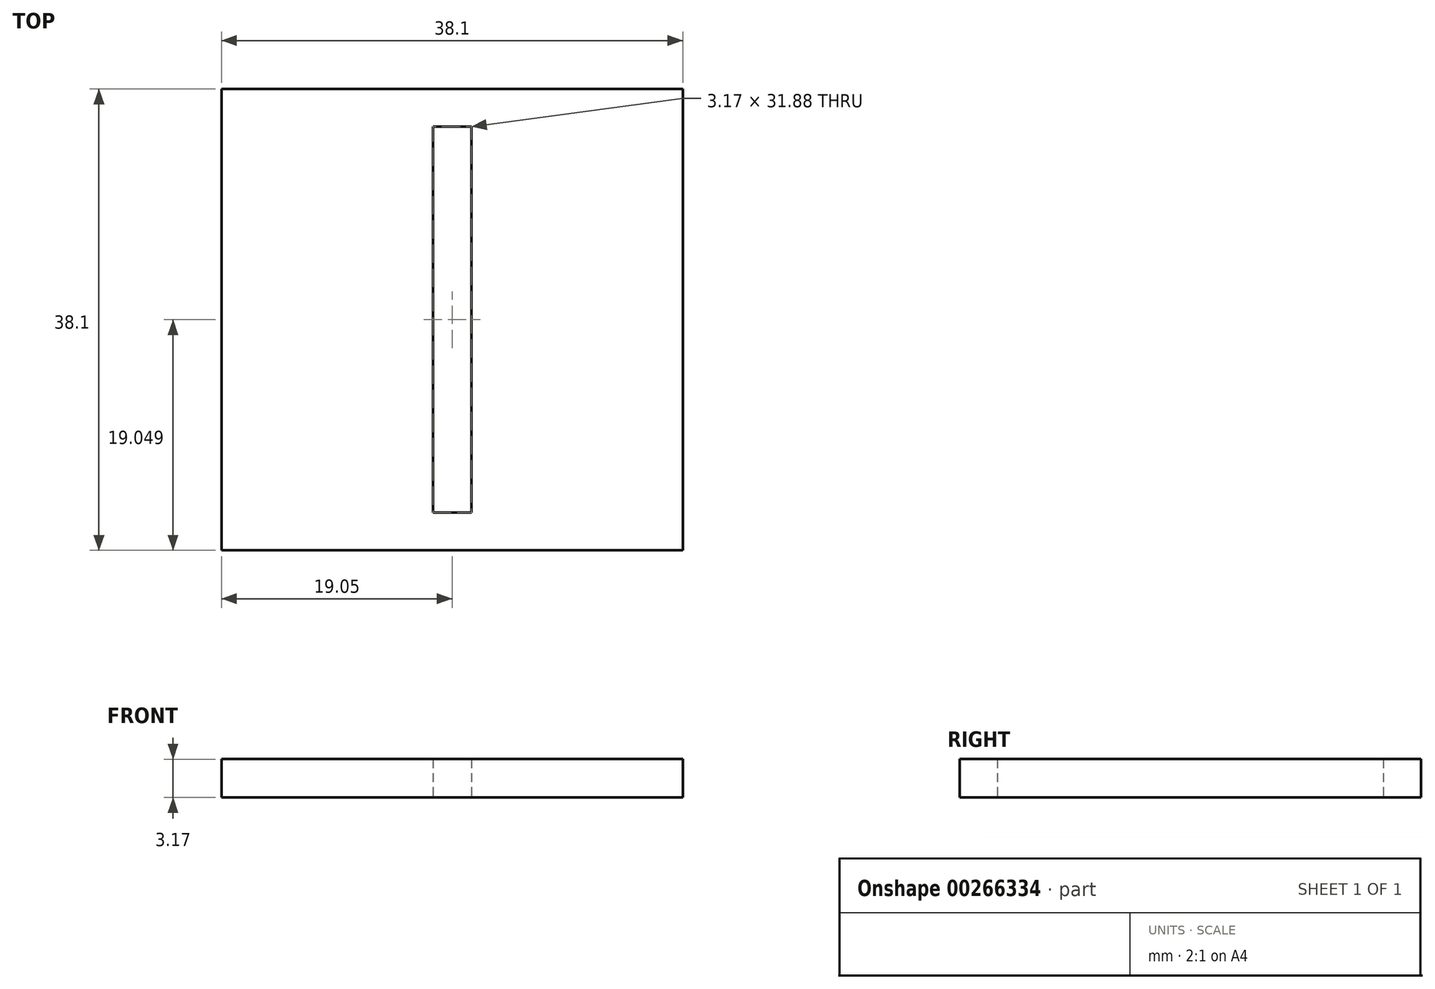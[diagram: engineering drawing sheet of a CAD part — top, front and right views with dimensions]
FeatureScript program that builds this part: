
annotation { "Feature Type Name" : "Feature", "Feature Type Description" : "" }
export const myFeature = defineFeature(function(context is Context, id is Id, definition is map)
    precondition{}
    {
        {
            var Q0;
            Q0=qCreatedBy(makeId("Top.planeOp"),FACE);
            var sketch = newSketch(context, id + "F0", { "sketchPlane" : qUnion([Q0])});
            skLineSegment(sketch, "E0.bottom", {"start": v(-21.25, -23.81) * mm, "end": v(16.85, -23.81) * mm});
            skLineSegment(sketch, "E0.top", {"start": v(-21.25, 14.29) * mm, "end": v(16.85, 14.29) * mm});
            skLineSegment(sketch, "E0.left", {"start": v(-21.25, -23.81) * mm, "end": v(-21.25, 14.29) * mm});
            skLineSegment(sketch, "E0.right", {"start": v(16.85, -23.81) * mm, "end": v(16.85, 14.29) * mm});
            skLineSegment(sketch, "E1.bottom", {"start": v(-3.79, -20.7) * mm, "end": v(-0.61, -20.7) * mm});
            skLineSegment(sketch, "E1.top", {"start": v(-3.79, 11.18) * mm, "end": v(-0.61, 11.18) * mm});
            skLineSegment(sketch, "E1.left", {"start": v(-3.79, -20.7) * mm, "end": v(-3.79, 11.18) * mm});
            skLineSegment(sketch, "E1.right", {"start": v(-0.61, -20.7) * mm, "end": v(-0.61, 11.18) * mm});
            skSolve(sketch);
        }
        {
            var Q0;
            Q0=makeQuery(id+"F0.imprint","IMPRINT",FACE,{"disambiguationData":[TD([[makeQuery(id+"F0.imprint","IMPRINT",EDGE,{"derivedFrom":sQuery(id+"F0.wireOp",EDGE,"E0.bottom")}),1.0]])]});
            extrude(context, id + "F1", {"entities" : qUnion([Q0]), "depth" : 3.17 * mm, "offsetDistance" : 25.4 * mm});
        }
    });
